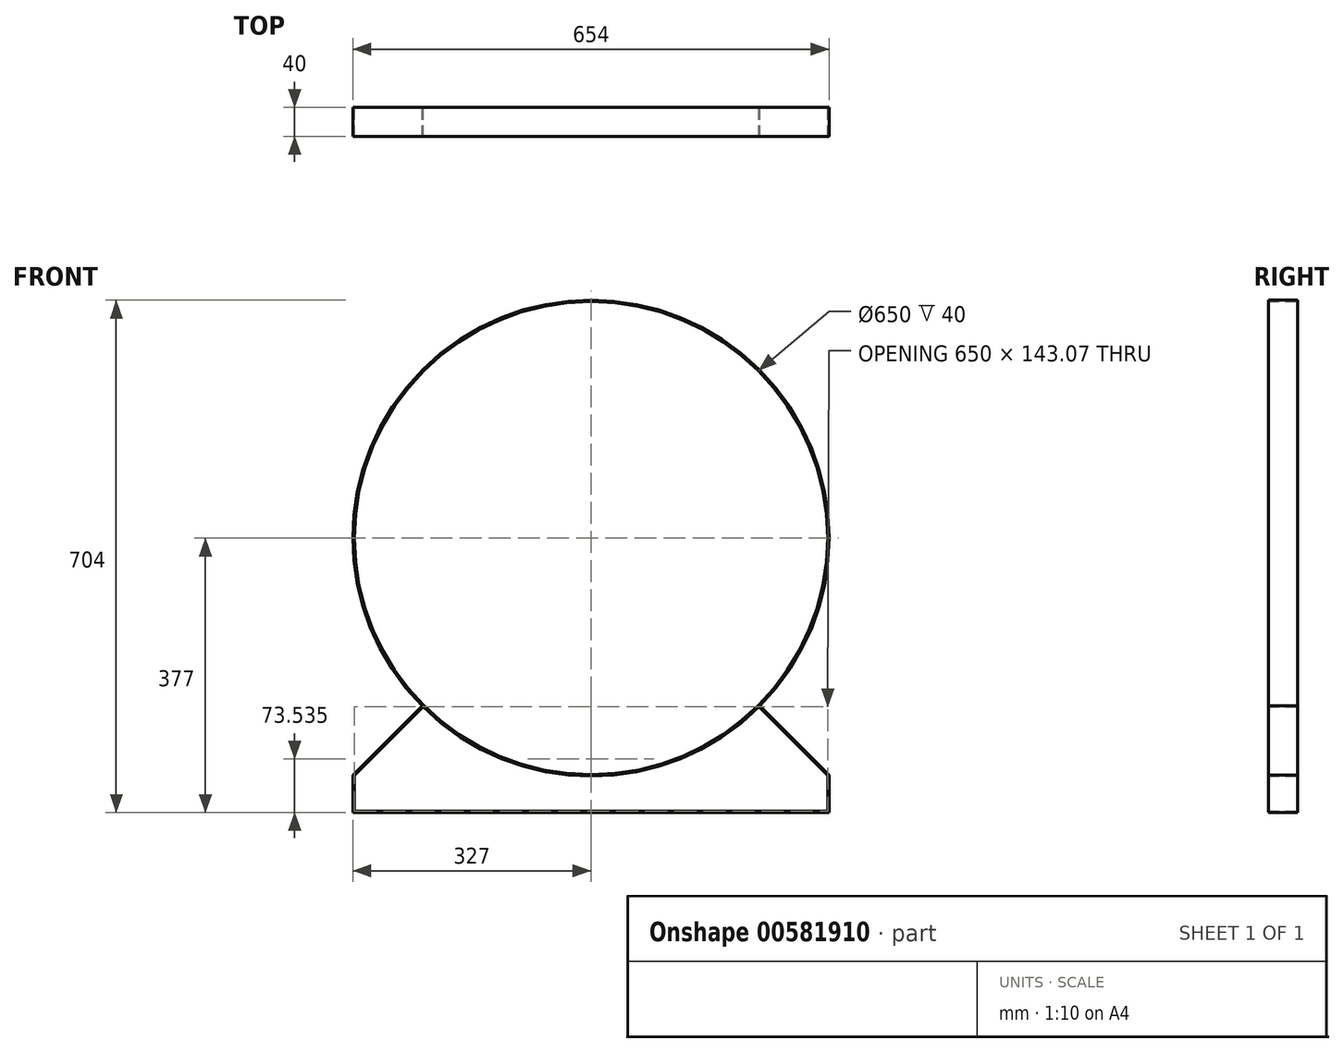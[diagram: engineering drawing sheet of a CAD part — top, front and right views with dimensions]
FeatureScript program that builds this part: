
annotation { "Feature Type Name" : "Feature", "Feature Type Description" : "" }
export const myFeature = defineFeature(function(context is Context, id is Id, definition is map)
    precondition{}
    {
        {
            var Q0;
            Q0=qCreatedBy(makeId("Front.planeOp"),FACE);
            var sketch = newSketch(context, id + "F0", { "sketchPlane" : qUnion([Q0])});
            skLineSegment(sketch, "E0", {"start": v(0, 0) * mm, "end": v(-679.96, 0) * mm, "construction": true});
            skLineSegment(sketch, "E1", {"start": v(0, 0) * mm, "end": v(0, 658.78) * mm, "construction": true});
            skLineSegment(sketch, "E2", {"start": v(0, 0) * mm, "end": v(-291.77, -291.77) * mm, "construction": true});
            skLineSegment(sketch, "E3", {"start": v(0, 0) * mm, "end": v(291.77, -291.77) * mm, "construction": true});
            skCircle(sketch, "E4", {"center": v(0, 0) * mm, "radius": 325 * mm});
            skCircle(sketch, "E5", {"center": v(0, 0) * mm, "radius": 327 * mm});
            skLineSegment(sketch, "E6", {"start": v(-327, -377) * mm, "end": v(0, -377) * mm});
            skLineSegment(sketch, "E7", {"start": v(-325, -375) * mm, "end": v(0, -375) * mm});
            skLineSegment(sketch, "E8", {"start": v(0, 0) * mm, "end": v(0, -311.11) * mm, "construction": true});
            skLineSegment(sketch, "E9", {"start": v(-325, -375) * mm, "end": v(-325, -326.41) * mm});
            skLineSegment(sketch, "E10", {"start": v(-327, -377) * mm, "end": v(-327, -325.59) * mm});
            skLineSegment(sketch, "E11", {"start": v(-231.93, -230.52) * mm, "end": v(-327, -325.59) * mm});
            skLineSegment(sketch, "E12", {"start": v(-230.52, -231.93) * mm, "end": v(-325, -326.41) * mm});
            skLineSegment(sketch, "E13.MirrorCS", {"start": v(230.52, -231.93) * mm, "end": v(325, -326.41) * mm});
            skLineSegment(sketch, "E14.MirrorCS", {"start": v(327, -377) * mm, "end": v(0, -377) * mm});
            skLineSegment(sketch, "E15.MirrorCS", {"start": v(325, -375) * mm, "end": v(0, -375) * mm});
            skLineSegment(sketch, "E16.MirrorCS", {"start": v(231.93, -230.52) * mm, "end": v(327, -325.59) * mm});
            skLineSegment(sketch, "E17.MirrorCS", {"start": v(325, -375) * mm, "end": v(325, -326.41) * mm});
            skLineSegment(sketch, "E18.MirrorCS", {"start": v(327, -377) * mm, "end": v(327, -325.59) * mm});
            skSolve(sketch);
        }
        {
            var Q0;
            Q0=qSketchRegion(id+"F0",true);
            extrude(context, id + "F1", {"entities" : qUnion([Q0]), "offsetDistance" : 25 * mm, "depth" : 40 * mm});
        }
    });
